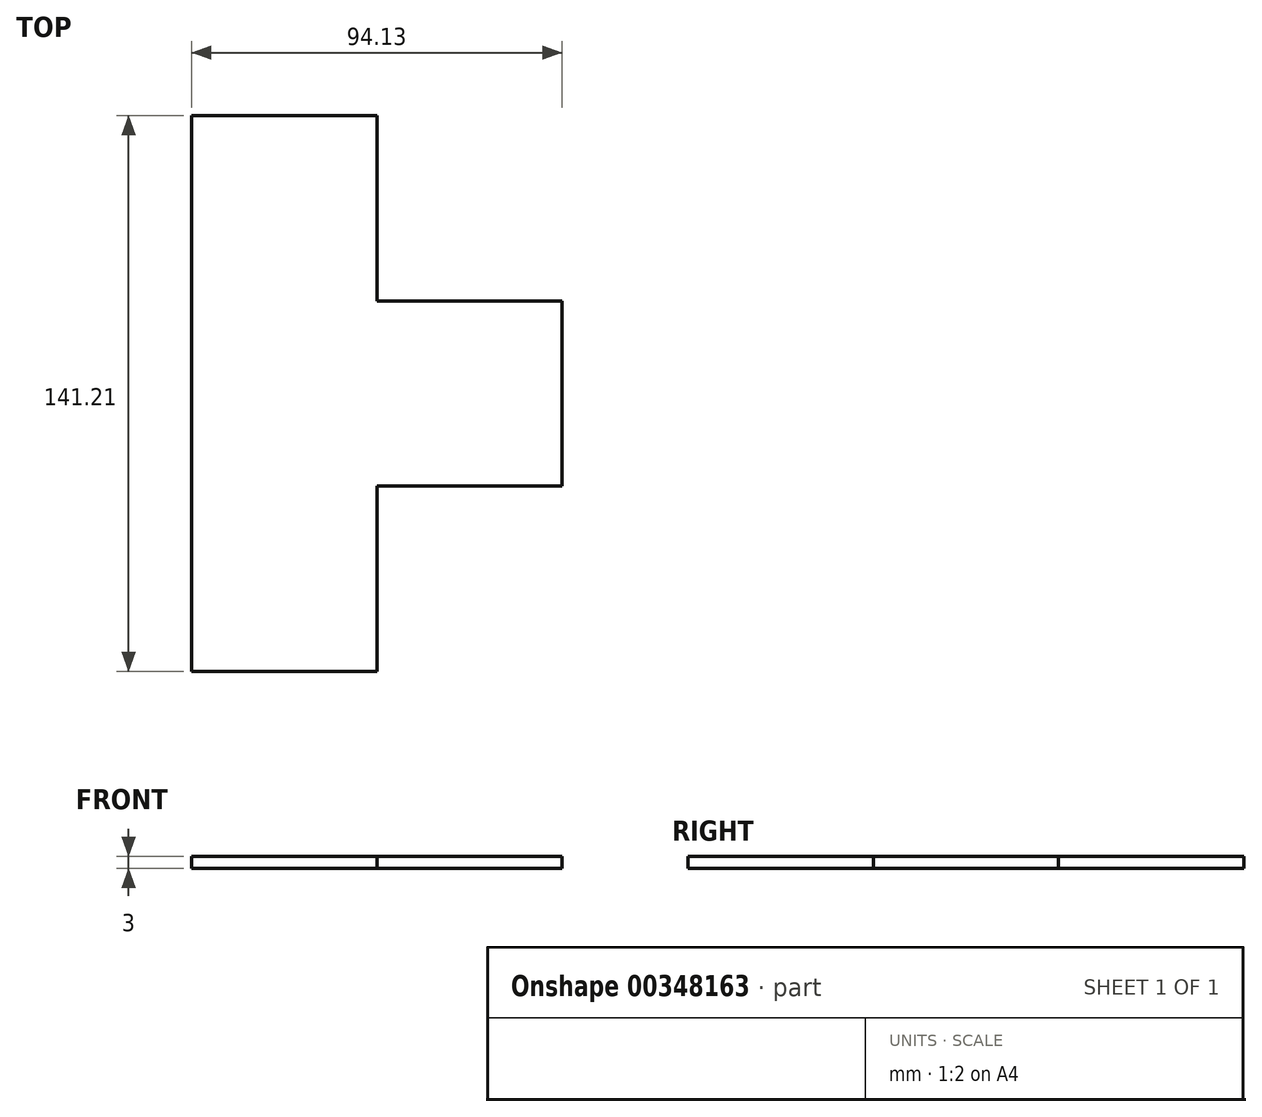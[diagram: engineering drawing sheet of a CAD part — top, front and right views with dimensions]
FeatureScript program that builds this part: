
annotation { "Feature Type Name" : "Feature", "Feature Type Description" : "" }
export const myFeature = defineFeature(function(context is Context, id is Id, definition is map)
    precondition{}
    {
        {
            var Q0;
            Q0=qCreatedBy(makeId("Top.planeOp"),FACE);
            var sketch = newSketch(context, id + "F0", { "sketchPlane" : qUnion([Q0])});
            skLineSegment(sketch, "E0.bottom", {"start": v(-39.2, 29.6) * mm, "end": v(54.94, 29.6) * mm});
            skLineSegment(sketch, "E0.left", {"start": v(-39.2, 29.6) * mm, "end": v(-39.2, -17.46) * mm});
            skLineSegment(sketch, "E0.right", {"start": v(54.94, 29.6) * mm, "end": v(54.94, -17.46) * mm});
            skLineSegment(sketch, "E1.bottom", {"start": v(-39.2, -17.46) * mm, "end": v(7.88, -17.46) * mm});
            skLineSegment(sketch, "E1.top", {"start": v(-39.2, -64.53) * mm, "end": v(7.88, -64.53) * mm});
            skLineSegment(sketch, "E1.left", {"start": v(-39.2, -17.46) * mm, "end": v(-39.2, -64.53) * mm});
            skLineSegment(sketch, "E1.right", {"start": v(7.88, -17.46) * mm, "end": v(7.88, -64.53) * mm});
            skLineSegment(sketch, "E2.bottom", {"start": v(-39.2, 29.6) * mm, "end": v(7.88, 29.6) * mm});
            skLineSegment(sketch, "E2.top", {"start": v(-39.2, 76.68) * mm, "end": v(7.88, 76.68) * mm});
            skLineSegment(sketch, "E2.left", {"start": v(-39.2, 29.6) * mm, "end": v(-39.2, 76.68) * mm});
            skLineSegment(sketch, "E2.right", {"start": v(7.88, 29.6) * mm, "end": v(7.88, 76.68) * mm});
            skLineSegment(sketch, "E3", {"start": v(54.94, -17.46) * mm, "end": v(7.88, -17.46) * mm});
            skSolve(sketch);
        }
        {
            var Q0;
            Q0=makeQuery(id+"F0.imprint","IMPRINT",FACE,{"disambiguationData":[TD([[makeQuery(id+"F0.imprint","IMPRINT",EDGE,{"derivedFrom":sQuery(id+"F0.wireOp",EDGE,"E2.top")}),-1.0]])]});
            var Q1;
            {var subQ5=sQuery(id+"F0.wireOp",EDGE,"E0.left");Q1=makeQuery(id+"F0.imprint","IMPRINT",FACE,{"disambiguationData":[TD([[makeQuery(id+"F0.imprint","IMPRINT",EDGE,{"derivedFrom":subQ5}),1.0]])]});}
            var Q2;
            Q2=makeQuery(id+"F0.imprint","IMPRINT",FACE,{"disambiguationData":[TD([[makeQuery(id+"F0.imprint","IMPRINT",EDGE,{"derivedFrom":sQuery(id+"F0.wireOp",EDGE,"E1.top")}),1.0]])]});
            extrude(context, id + "F1", {"entities" : qUnion([Q0, Q1, Q2]), "depth" : 3 * mm, "offsetDistance" : 25.4 * mm});
        }
    });
